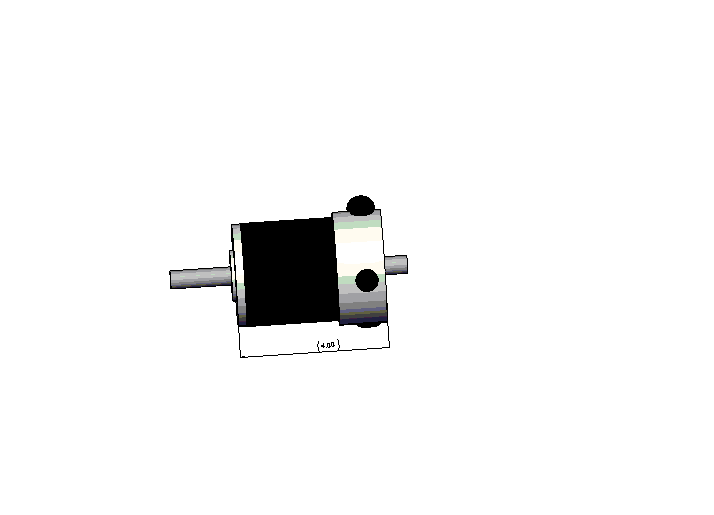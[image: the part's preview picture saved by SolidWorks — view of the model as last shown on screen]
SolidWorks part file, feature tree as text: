
SOLIDWORKS PART (.sldprt)
format: sldprt  version: not decoded by parser v0  size: 343,552 bytes
history: native  units: mm
features: sketch x14, extrude x11, plane x6, fillet x1 + 1 further entry (+6 scaffold rows collapsed)
feature tree (39):
  "Annotations"  RD1=101.6mm
  scaffold x6  (default folders/planes/origin — collapsed)
  plane  "Plane1"
  plane  "Plane2"
  plane  "Plane3"
  sketch  "Sketch1"  dims[D1=~4.063954mm]
  extrude  "Base-Extrude"  Depth=95.758mm
  sketch  "Sketch2"  dims[D1=~49.595085mm]
  extrude  "Boss-Extrude1"  Depth=32.766mm
  sketch  "Sketch3"  dims[D1=~8.980256mm]
  extrude  "Boss-Extrude2"  Depth=49.784mm
  sketch  "Sketch4"  dims[D1=~13.73715mm]
  extrude  "Boss-Extrude3"  Depth=8.382mm
  sketch  "Sketch5"
  sketch  "Sketch6"
  plane  "Plane4"
  sketch  "Sketch7"  dims[D1=~9.919017mm]
  extrude  "Boss-Extrude5"  Depth=40.386mm
  sketch  "Sketch9"
  extrude  "Boss-Extrude7"  Depth=80.772mm
  sketch  "Sketch10"
  plane  "Plane5"
  sketch  "Sketch11"  dims[D1=12.5095mm]
  extrude  "Boss-Extrude8"  Depth=40.386mm
  sketch  "Sketch12"  dims[D1=12.5095mm]
  extrude  "Boss-Extrude10"  Depth=80.772mm
  plane  "Plane6"
  sketch  "Sketch13"  dims[D1=36.83mm]
  extrude  "Boss-Extrude11"  Depth=53.975mm
  fillet  "Fillet1"  Radius=6.35mm
  sketch  "Sketch14"  dims[D1=~7.405309mm]
  extrude  "Boss-Extrude12"  Depth=16.002mm
  sketch  "Sketch15"  dims[D1=35.306mm]
  extrude  "Boss-Extrude13"  Depth=5.842mm
decode coverage: 22 of 26 modeling features carry decoded parameters; 1 rows unclassified (native names shown)
note: ~ marks probable driven/reference dimensions
note: suppression state not decoded; provenance and decode notes live in map.json
